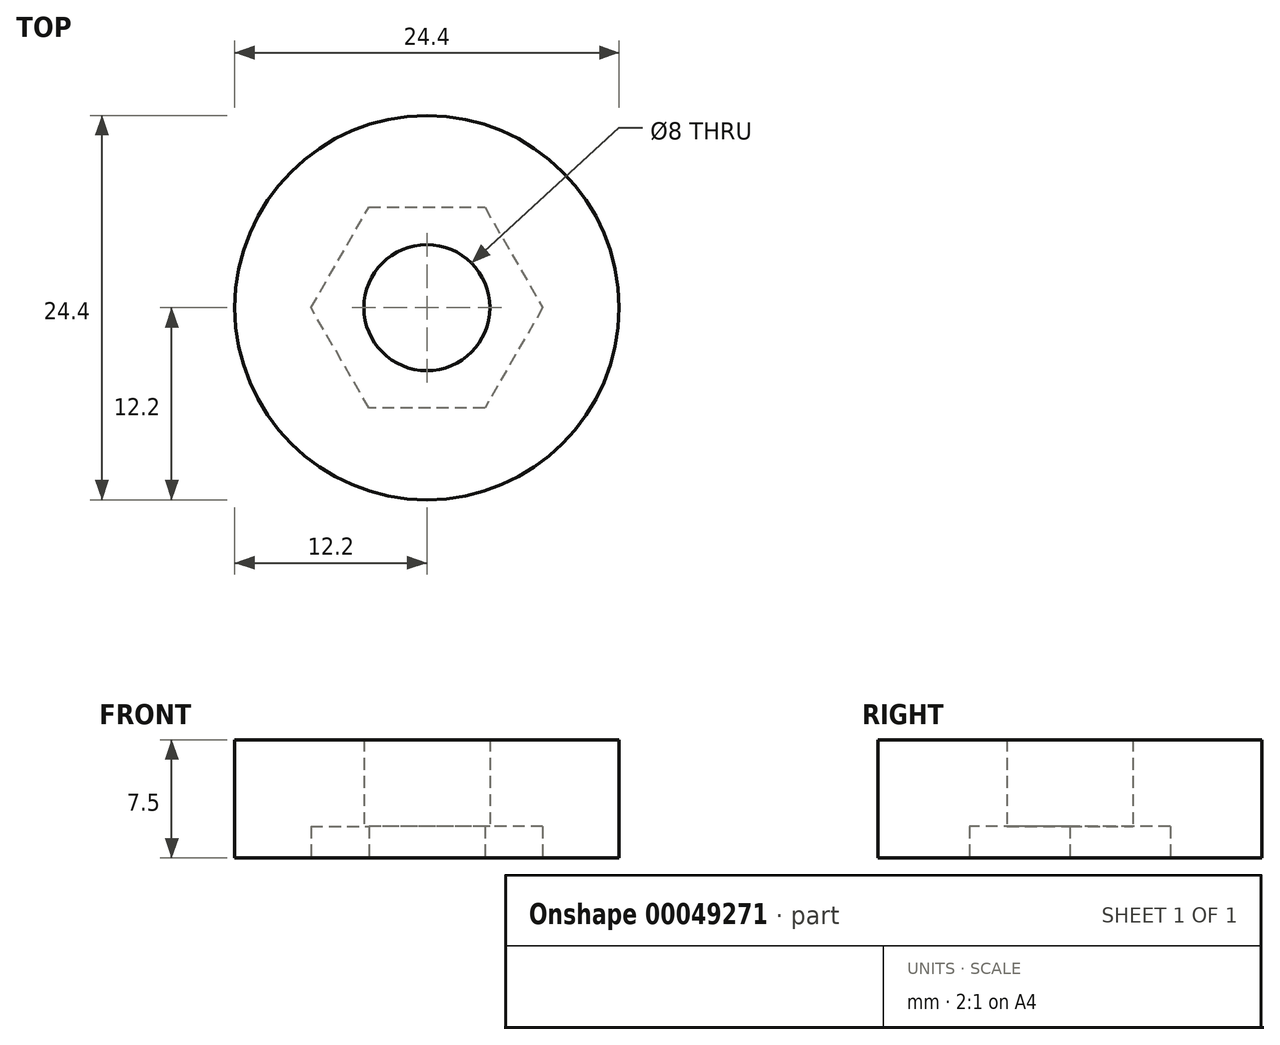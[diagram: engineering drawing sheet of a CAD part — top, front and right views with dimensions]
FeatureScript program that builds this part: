
annotation { "Feature Type Name" : "Feature", "Feature Type Description" : "" }
export const myFeature = defineFeature(function(context is Context, id is Id, definition is map)
    precondition{}
    {
        {
            var Q0;
            Q0=qCreatedBy(makeId("Top.planeOp"),FACE);
            var sketch = newSketch(context, id + "F0", { "sketchPlane" : qUnion([Q0])});
            skCircle(sketch, "E0", {"center": v(0, 0) * mm, "radius": 13.5 * mm, "construction": true});
            skCircle(sketch, "E1.0", {"center": v(0, 0) * mm, "radius": 12.2 * mm});
            skCircle(sketch, "E2", {"center": v(0, 0) * mm, "radius": 4 * mm});
            skCircle(sketch, "E3.cCircle", {"center": v(0, 0) * mm, "radius": 6.38 * mm, "construction": true});
            skLineSegment(sketch, "E3.0", {"start": v(3.68, -6.38) * mm, "end": v(-3.68, -6.38) * mm});
            skLineSegment(sketch, "E3.1", {"start": v(-3.68, -6.38) * mm, "end": v(-7.36, 0) * mm});
            skLineSegment(sketch, "E3.2", {"start": v(-7.36, 0) * mm, "end": v(-3.68, 6.37) * mm});
            skLineSegment(sketch, "E3.3", {"start": v(-3.68, 6.38) * mm, "end": v(3.68, 6.38) * mm});
            skLineSegment(sketch, "E3.4", {"start": v(3.68, 6.38) * mm, "end": v(7.36, 0) * mm});
            skLineSegment(sketch, "E3.5", {"start": v(7.36, 0) * mm, "end": v(3.68, -6.37) * mm});
            skPoint(sketch, "E3.0.midPoint", {"position": v(0, -6.38) * mm});
            skSolve(sketch);
        }
        {
            var Q0;
            Q0=makeQuery(id+"F0.imprint","IMPRINT",FACE,{"disambiguationData":[TD([[makeQuery(id+"F0.imprint","IMPRINT",EDGE,{"derivedFrom":sQuery(id+"F0.wireOp",EDGE,"E1.0")}),1.0]])]});
            var Q1;
            Q1=makeQuery(id+"F0.imprint","IMPRINT",FACE,{"disambiguationData":[TD([[makeQuery(id+"F0.imprint","IMPRINT",EDGE,{"derivedFrom":sQuery(id+"F0.wireOp",EDGE,"E2")}),-1.0]])]});
            extrude(context, id + "F1", {"entities" : qUnion([Q0, Q1]), "depth" : 7.5 * mm});
        }
        {
            var Q0;
            Q0=makeQuery(id+"F0.imprint","IMPRINT",FACE,{"disambiguationData":[TD([[makeQuery(id+"F0.imprint","IMPRINT",EDGE,{"derivedFrom":sQuery(id+"F0.wireOp",EDGE,"E2")}),1.0]])]});
            var Q1;
            Q1=makeQuery(id+"F0.imprint","IMPRINT",FACE,{"disambiguationData":[TD([[makeQuery(id+"F0.imprint","IMPRINT",EDGE,{"derivedFrom":sQuery(id+"F0.wireOp",EDGE,"E2")}),-1.0]])]});
            extrude(context, id + "F2", {"entities" : qUnion([Q0, Q1]), "operationType" : NewBodyOperationType.REMOVE, "depth" : 2 * mm});
        }
    });
